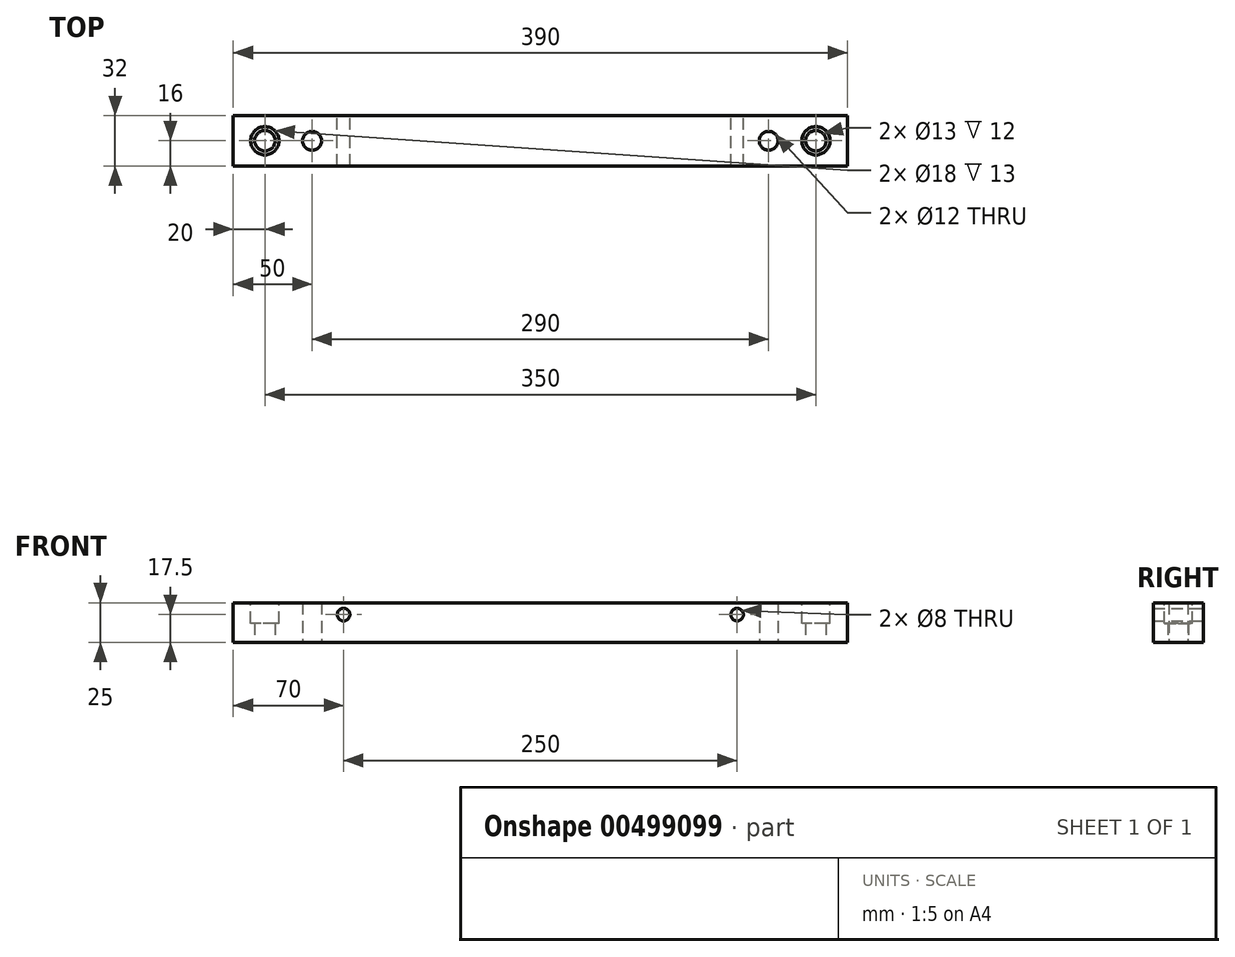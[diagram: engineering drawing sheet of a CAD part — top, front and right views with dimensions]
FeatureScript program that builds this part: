
annotation { "Feature Type Name" : "Feature", "Feature Type Description" : "" }
export const myFeature = defineFeature(function(context is Context, id is Id, definition is map)
    precondition{}
    {
        {
            var Q0;
            Q0=qCreatedBy(makeId("Right.planeOp"),FACE);
            var sketch = newSketch(context, id + "F0", { "sketchPlane" : qUnion([Q0])});
            skLineSegment(sketch, "E0.bottom", {"start": v(16, -12.5) * mm, "end": v(-16, -12.5) * mm});
            skLineSegment(sketch, "E0.top", {"start": v(16, 12.5) * mm, "end": v(-16, 12.5) * mm});
            skLineSegment(sketch, "E0.left", {"start": v(16, -12.5) * mm, "end": v(16, 12.5) * mm});
            skLineSegment(sketch, "E0.right", {"start": v(-16, -12.5) * mm, "end": v(-16, 12.5) * mm});
            skPoint(sketch, "E0.middle", {"position": v(0, 0) * mm});
            skSolve(sketch);
        }
        {
            var Q0;
            Q0=makeQuery(id+"F0.imprint","IMPRINT",FACE,{"disambiguationData":[TD([[makeQuery(id+"F0.imprint","IMPRINT",EDGE,{"derivedFrom":sQuery(id+"F0.wireOp",EDGE,"E0.bottom")}),-1.0]])]});
            extrude(context, id + "F1", {"entities" : qUnion([Q0]), "depth" : 390 * mm});
        }
        {
            var Q0;
            Q0=makeQuery(id+"F1.opExtrude","SWEPT_FACE",FACE,{"disambiguationData":[OSD([sQuery(id+"F0.wireOp",EDGE,"E0.left")])]});
            var sketch = newSketch(context, id + "F2", { "sketchPlane" : qUnion([Q0])});
            skCircle(sketch, "E1", {"center": v(-320, 5) * mm, "radius": 4 * mm});
            skCircle(sketch, "E2", {"center": v(-70, 5) * mm, "radius": 4 * mm});
            skSolve(sketch);
        }
        {
            var Q0;
            Q0 = qSketchRegion(id + "F2", true);
            extrude(context, id + "F3", {"entities" : qUnion([Q0]), "operationType" : NewBodyOperationType.REMOVE, "oppositeDirection" : true, "depth" : 93 * mm});
        }
        {
            var Q0;
            Q0=makeQuery(id+"F1.opExtrude","SWEPT_FACE",FACE,{"disambiguationData":[OSD([sQuery(id+"F0.wireOp",EDGE,"E0.bottom")])]});
            var sketch = newSketch(context, id + "F4", { "sketchPlane" : qUnion([Q0])});
            skCircle(sketch, "E3", {"center": v(20, 0) * mm, "radius": 6.5 * mm});
            skCircle(sketch, "E4", {"center": v(370, 0) * mm, "radius": 6.5 * mm});
            skSolve(sketch);
        }
        {
            var Q0;
            Q0 = qSketchRegion(id + "F4", true);
            extrude(context, id + "F5", {"entities" : qUnion([Q0]), "operationType" : NewBodyOperationType.REMOVE, "oppositeDirection" : true, "depth" : 40.8 * mm});
        }
        {
            var Q0;
            Q0=makeQuery(id+"F1.opExtrude","SWEPT_FACE",FACE,{"disambiguationData":[OSD([sQuery(id+"F0.wireOp",EDGE,"E0.top")])]});
            var sketch = newSketch(context, id + "F6", { "sketchPlane" : qUnion([Q0])});
            skCircle(sketch, "E5", {"center": v(20, 0) * mm, "radius": 9 * mm});
            skCircle(sketch, "E6", {"center": v(370, 0) * mm, "radius": 9 * mm});
            skSolve(sketch);
        }
        {
            var Q0;
            Q0 = qSketchRegion(id + "F6", true);
            extrude(context, id + "F7", {"entities" : qUnion([Q0]), "operationType" : NewBodyOperationType.REMOVE, "oppositeDirection" : true, "depth" : 13 * mm});
        }
        {
            var Q0;
            Q0=makeQuery(id+"F1.opExtrude","SWEPT_FACE",FACE,{"disambiguationData":[OSD([sQuery(id+"F0.wireOp",EDGE,"E0.bottom")])]});
            var sketch = newSketch(context, id + "F8", { "sketchPlane" : qUnion([Q0])});
            skCircle(sketch, "E7", {"center": v(50, 0) * mm, "radius": 6 * mm});
            skCircle(sketch, "E8", {"center": v(340, 0) * mm, "radius": 6 * mm});
            skSolve(sketch);
        }
        {
            var Q0;
            Q0 = qSketchRegion(id + "F8", true);
            extrude(context, id + "F9", {"entities" : qUnion([Q0]), "operationType" : NewBodyOperationType.REMOVE, "oppositeDirection" : true, "depth" : 76.1 * mm});
        }
    });
